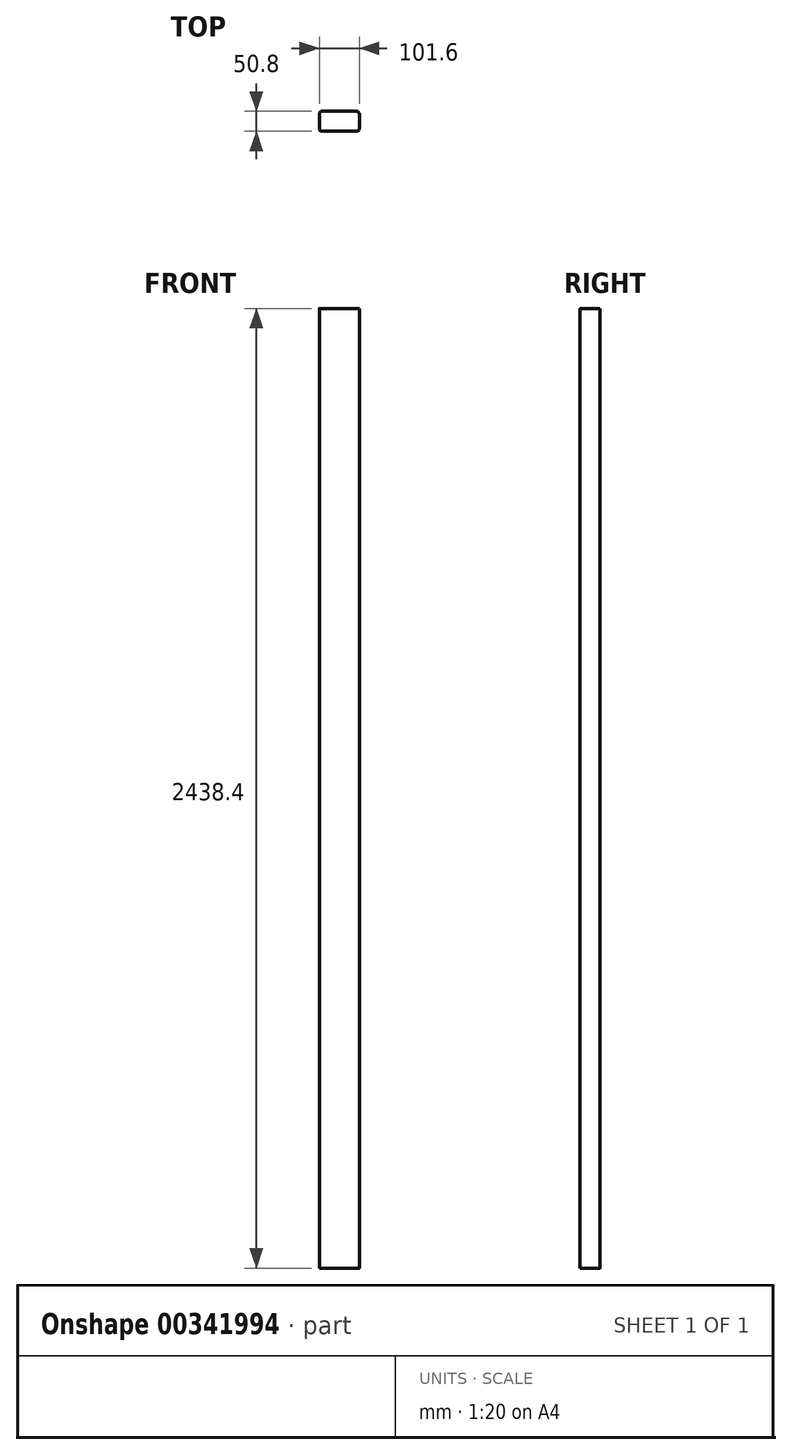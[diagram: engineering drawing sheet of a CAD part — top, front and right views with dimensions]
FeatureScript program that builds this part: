
annotation { "Feature Type Name" : "Feature", "Feature Type Description" : "" }
export const myFeature = defineFeature(function(context is Context, id is Id, definition is map)
    precondition{}
    {
        {
            var Q0;
            Q0=qCreatedBy(makeId("Top.planeOp"),FACE);
            var sketch = newSketch(context, id + "F0", { "sketchPlane" : qUnion([Q0])});
            skLineSegment(sketch, "E0.bottom", {"start": v(6.35, 0) * mm, "end": v(95.25, 0) * mm});
            skLineSegment(sketch, "E0.top", {"start": v(6.35, 50.8) * mm, "end": v(95.25, 50.8) * mm});
            skLineSegment(sketch, "E0.left", {"start": v(0, 6.35) * mm, "end": v(0, 44.45) * mm});
            skLineSegment(sketch, "E0.right", {"start": v(101.6, 6.35) * mm, "end": v(101.6, 44.45) * mm});
            skPoint(sketch, "E1.visualSharp", {"position": v(0, 50.8) * mm});
            skArc(sketch, "E1.filletArc", {"start": v(6.35, 50.8) * mm, "mid": v(1.86, 48.94) * mm, "end": v(0, 44.45) * mm});
            skPoint(sketch, "E2.visualSharp", {"position": v(0, 0) * mm});
            skArc(sketch, "E2.filletArc", {"start": v(0, 6.35) * mm, "mid": v(1.86, 1.86) * mm, "end": v(6.35, 0) * mm});
            skPoint(sketch, "E3.visualSharp", {"position": v(101.6, 0) * mm});
            skArc(sketch, "E3.filletArc", {"start": v(95.25, 0) * mm, "mid": v(99.74, 1.86) * mm, "end": v(101.6, 6.35) * mm});
            skPoint(sketch, "E4.visualSharp", {"position": v(101.6, 50.8) * mm});
            skArc(sketch, "E4.filletArc", {"start": v(101.6, 44.45) * mm, "mid": v(99.74, 48.94) * mm, "end": v(95.25, 50.8) * mm});
            skSolve(sketch);
        }
        {
            var Q0;
            Q0=makeQuery(id+"F0.imprint","IMPRINT",FACE,{"disambiguationData":[TD([[makeQuery(id+"F0.imprint","IMPRINT",EDGE,{"derivedFrom":sQuery(id+"F0.wireOp",EDGE,"E0.bottom")}),1.0]])]});
            extrude(context, id + "F1", {"entities" : qUnion([Q0]), "depth" : 2438.4 * mm});
        }
    });
